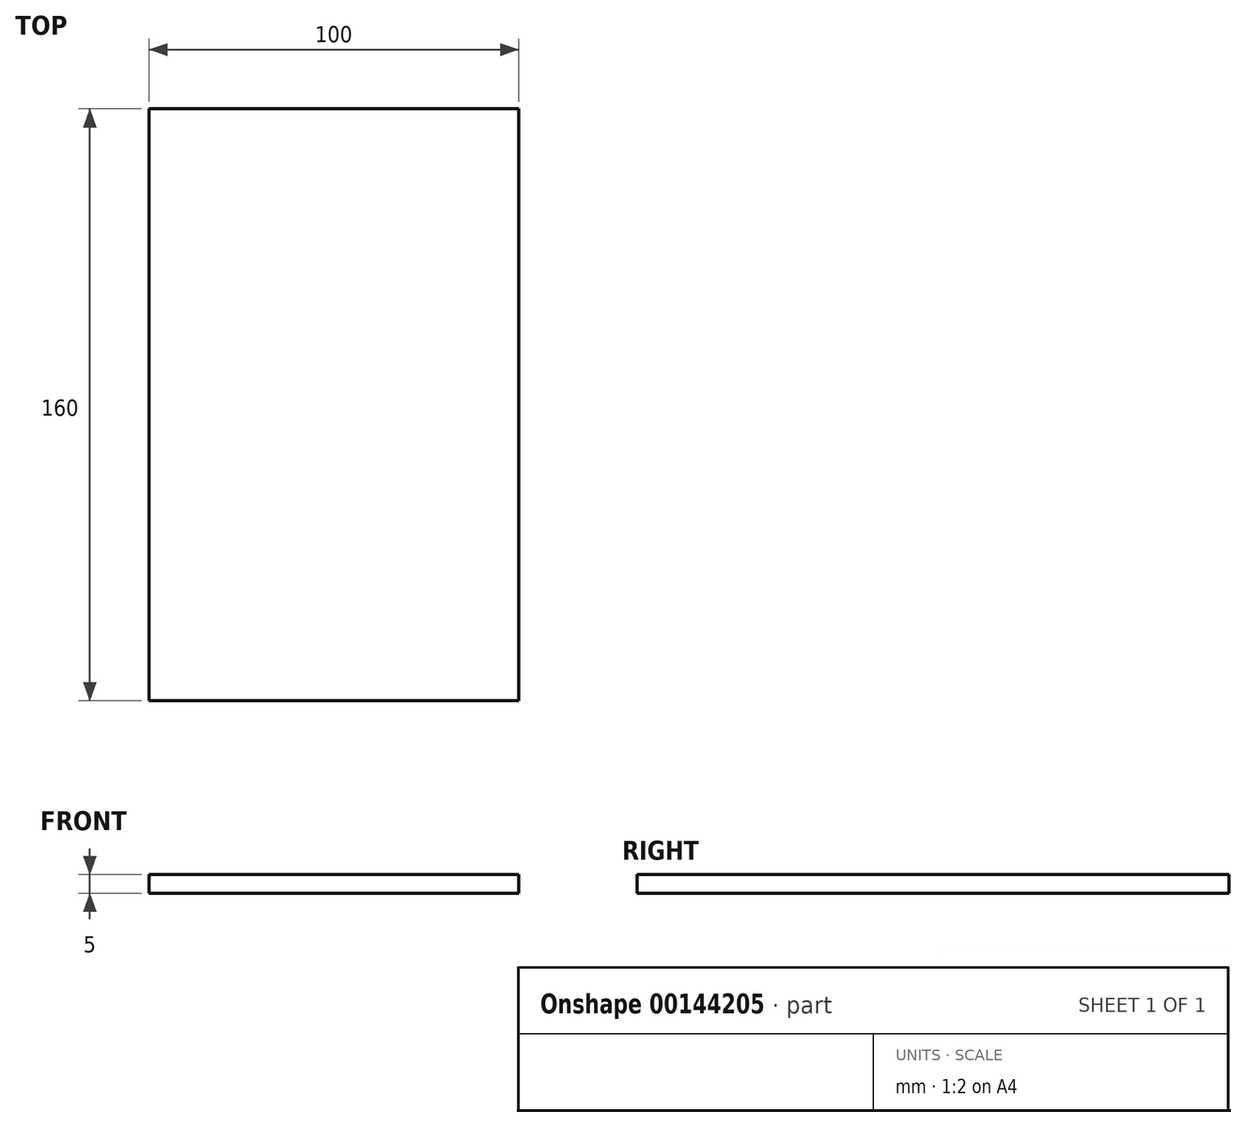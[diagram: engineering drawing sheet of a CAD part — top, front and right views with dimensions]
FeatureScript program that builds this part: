
annotation { "Feature Type Name" : "Feature", "Feature Type Description" : "" }
export const myFeature = defineFeature(function(context is Context, id is Id, definition is map)
    precondition{}
    {
        {
            var Q0;
            Q0=qCreatedBy(makeId("Top.planeOp"),FACE);
            var sketch = newSketch(context, id + "F0", { "sketchPlane" : qUnion([Q0])});
            skLineSegment(sketch, "E0.bottom", {"start": v(0, 0) * mm, "end": v(100, 0) * mm});
            skLineSegment(sketch, "E0.top", {"start": v(0, 160) * mm, "end": v(100, 160) * mm});
            skLineSegment(sketch, "E0.left", {"start": v(0, 0) * mm, "end": v(0, 160) * mm});
            skLineSegment(sketch, "E0.right", {"start": v(100, 0) * mm, "end": v(100, 160) * mm});
            skSolve(sketch);
        }
        {
            var Q0;
            Q0=makeQuery(id+"F0.imprint","IMPRINT",FACE,{"disambiguationData":[TD([[makeQuery(id+"F0.imprint","IMPRINT",EDGE,{"derivedFrom":sQuery(id+"F0.wireOp",EDGE,"E0.bottom")}),1.0]])]});
            extrude(context, id + "F1", {"entities" : qUnion([Q0]), "depth" : 5 * mm});
        }
    });
